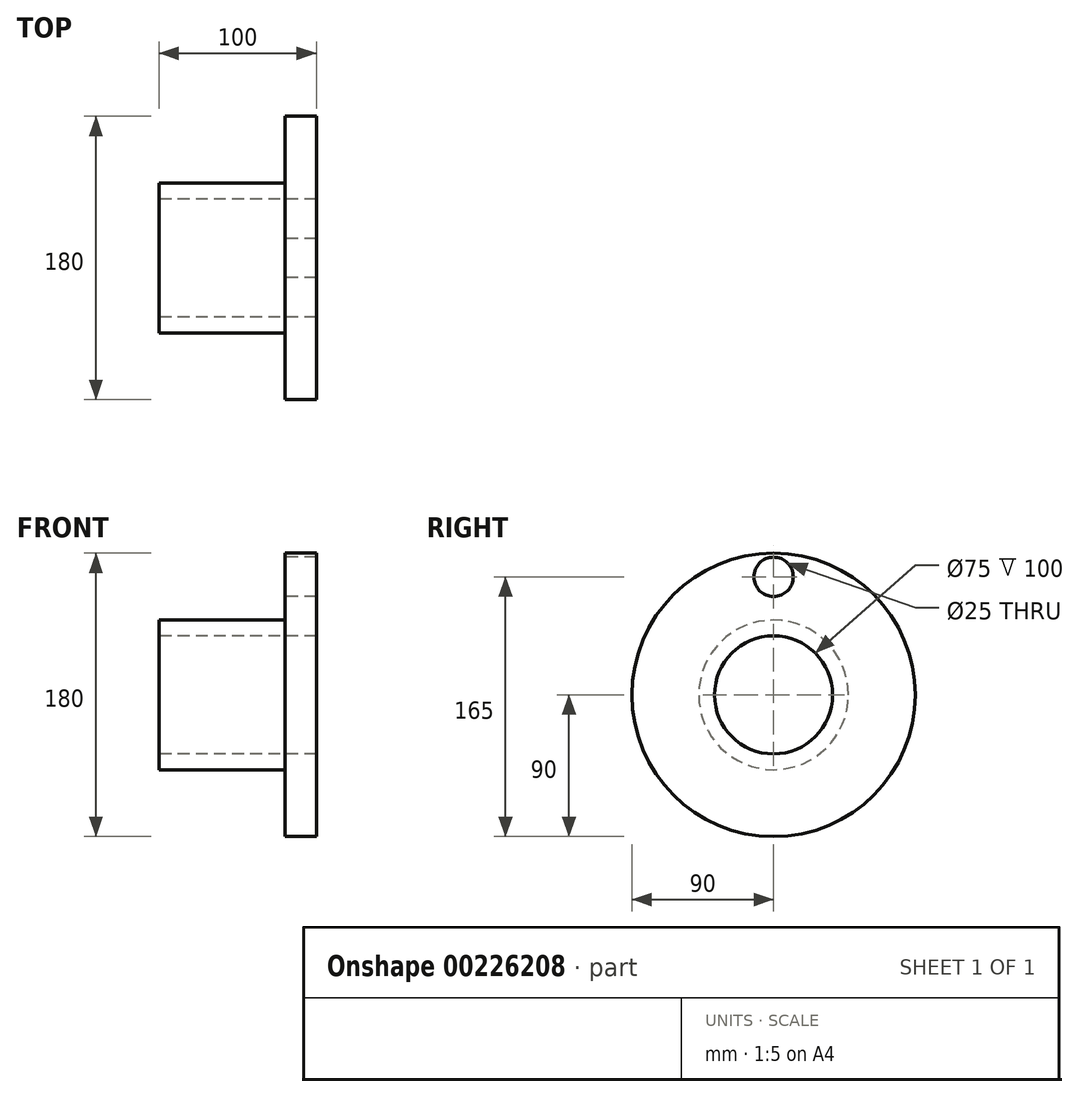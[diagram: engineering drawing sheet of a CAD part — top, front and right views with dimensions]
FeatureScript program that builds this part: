
annotation { "Feature Type Name" : "Feature", "Feature Type Description" : "" }
export const myFeature = defineFeature(function(context is Context, id is Id, definition is map)
    precondition{}
    {
        {
            var Q0;
            Q0=qCreatedBy(makeId("Front.planeOp"),FACE);
            var sketch = newSketch(context, id + "F0", { "sketchPlane" : qUnion([Q0])});
            skLineSegment(sketch, "E0", {"start": v(-121.15, 0) * mm, "end": v(0, 0) * mm, "construction": true});
            skLineSegment(sketch, "E1", {"start": v(0, 37.5) * mm, "end": v(0, 90) * mm});
            skLineSegment(sketch, "E2", {"start": v(0, 90) * mm, "end": v(-20, 90) * mm});
            skLineSegment(sketch, "E3", {"start": v(-20, 90) * mm, "end": v(-20, 47.5) * mm});
            skLineSegment(sketch, "E4", {"start": v(-100, 47.5) * mm, "end": v(-20, 47.5) * mm});
            skLineSegment(sketch, "E5", {"start": v(-100, 47.5) * mm, "end": v(-100, 37.5) * mm});
            skLineSegment(sketch, "E6", {"start": v(-100, 37.5) * mm, "end": v(0, 37.5) * mm});
            skSolve(sketch);
        }
        {
            var Q0;
            Q0=makeQuery(id+"F0.imprint","IMPRINT",FACE,{"disambiguationData":[TD([[makeQuery(id+"F0.imprint","IMPRINT",EDGE,{"derivedFrom":sQuery(id+"F0.wireOp",EDGE,"E1")}),1.0]])]});
            var Q1;
            Q1=sQuery(id+"F0.wireOp",EDGE,"E0");
            revolve(context, id + "F1", {"entities" : qUnion([Q0]), "axis" : qUnion([Q1]), "revolveType" : RevolveType.FULL});
        }
        {
            var Q0;
            Q0=makeQuery(id+"F1.opRevolve","SWEPT_FACE",FACE,{"disambiguationData":[OSD([sQuery(id+"F0.wireOp",EDGE,"E3")])]});
            var sketch = newSketch(context, id + "F2", { "sketchPlane" : qUnion([Q0])});
            skCircle(sketch, "E7", {"center": v(0, 75) * mm, "radius": 12.5 * mm});
            skSolve(sketch);
        }
        {
            var Q0;
            Q0 = qSketchRegion(id + "F2", true);
            extrude(context, id + "F3", {"entities" : qUnion([Q0]), "operationType" : NewBodyOperationType.REMOVE, "oppositeDirection" : true, "depth" : 281 * mm});
        }
    });
